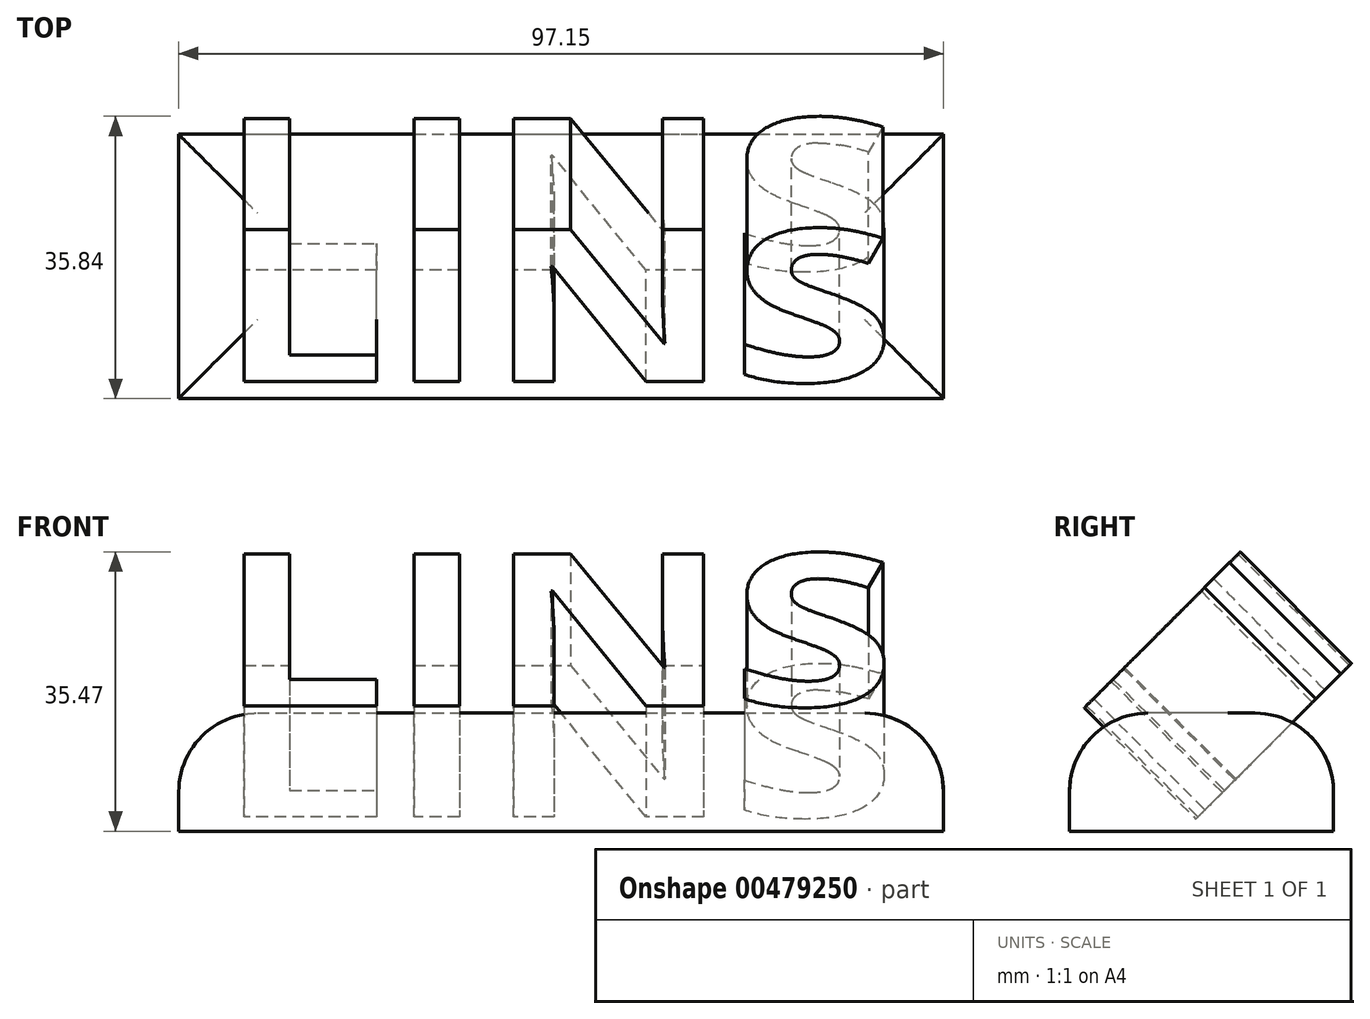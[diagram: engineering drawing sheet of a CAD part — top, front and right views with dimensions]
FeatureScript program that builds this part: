
annotation { "Feature Type Name" : "Feature", "Feature Type Description" : "" }
export const myFeature = defineFeature(function(context is Context, id is Id, definition is map)
    precondition{}
    {
        {
            var Q0;
            Q0=qCreatedBy(makeId("Top.planeOp"),FACE);
            var sketch = newSketch(context, id + "F0", { "sketchPlane" : qUnion([Q0])});
            skText(sketch, "E0", { "text": "LINS", "fontName": "OpenSans-Bold.ttf"});
            const initialGuessF0  = {"E0": [-0.04957, -0.04822, 1, 0, 0.02747]};
            skSetInitialGuess(sketch, initialGuessF0);
            skSolve(sketch);
        }
        {
            var Q0;
            Q0 = qSketchRegion(id + "F0", true);
            extrude(context, id + "F1", {"entities" : qUnion([Q0]), "depth" : 20 * mm});
        }
        {
            var Q0;
            Q0=qCreatedBy(makeId("Top.planeOp"),FACE);
            var sketch = newSketch(context, id + "F2", { "sketchPlane" : qUnion([Q0])});
            skLineSegment(sketch, "E1.bottom", {"start": v(-44.06, 21.02) * mm, "end": v(53.1, 21.02) * mm});
            skLineSegment(sketch, "E1.top", {"start": v(-44.06, -12.54) * mm, "end": v(53.1, -12.54) * mm});
            skLineSegment(sketch, "E1.left", {"start": v(-44.06, 21.02) * mm, "end": v(-44.06, -12.54) * mm});
            skLineSegment(sketch, "E1.right", {"start": v(53.1, 21.02) * mm, "end": v(53.1, -12.54) * mm});
            skSolve(sketch);
        }
        {
            var Q0;
            Q0=makeQuery(id+"F2.imprint","IMPRINT",FACE,{"disambiguationData":[TD([[makeQuery(id+"F2.imprint","IMPRINT",EDGE,{"derivedFrom":sQuery(id+"F2.wireOp",EDGE,"E1.bottom")}),-1.0]])]});
            extrude(context, id + "F3", {"entities" : qUnion([Q0]), "depth" : 15 * mm});
        }
        {
            var Q0;
            Q0=makeQuery(id+"F3.opExtrude","CAP_EDGE",EDGE,{"disambiguationData":[OSD([sQuery(id+"F2.wireOp",EDGE,"E1.left")])],"isStart":false});
            var Q1;
            Q1=makeQuery(id+"F3.opExtrude","CAP_EDGE",EDGE,{"disambiguationData":[OSD([sQuery(id+"F2.wireOp",EDGE,"E1.bottom")])],"isStart":false});
            var Q2;
            Q2=makeQuery(id+"F3.opExtrude","CAP_EDGE",EDGE,{"disambiguationData":[OSD([sQuery(id+"F2.wireOp",EDGE,"E1.right")])],"isStart":false});
            var Q3;
            Q3=makeQuery(id+"F3.opExtrude","CAP_EDGE",EDGE,{"disambiguationData":[OSD([sQuery(id+"F2.wireOp",EDGE,"E1.top")])],"isStart":false});
            fillet(context, id + "F4", {"entities" : qUnion([Q0, Q1, Q2, Q3]), "radius" : 10 * mm, "tangentPropagation" : true, "allowEdgeOverflow" : false});
        }
        {
            var Q0;
            Q0=makeQuery(id+"F1.opExtrude","SWEPT_BODY",BODY,{"disambiguationData":[OSD([sQuery(id+"F0.wireOp",EDGE,"E0.sketch_text.stroke-0"),sQuery(id+"F0.wireOp",EDGE,"E0.sketch_text.stroke-1"),sQuery(id+"F0.wireOp",EDGE,"E0.sketch_text.stroke-2"),sQuery(id+"F0.wireOp",EDGE,"E0.sketch_text.stroke-3"),sQuery(id+"F0.wireOp",EDGE,"E0.sketch_text.stroke-4"),sQuery(id+"F0.wireOp",EDGE,"E0.sketch_text.stroke-5"),sQuery(id+"F0.wireOp",EDGE,"E0.sketch_text.stroke-6"),sQuery(id+"F0.wireOp",EDGE,"E0.sketch_text.stroke-7"),sQuery(id+"F0.wireOp",EDGE,"E0.sketch_text.stroke-8"),sQuery(id+"F0.wireOp",EDGE,"E0.sketch_text.stroke-9"),sQuery(id+"F0.wireOp",EDGE,"E0.sketch_text.stroke-10"),sQuery(id+"F0.wireOp",EDGE,"E0.sketch_text.stroke-11"),sQuery(id+"F0.wireOp",EDGE,"E0.sketch_text.stroke-12"),sQuery(id+"F0.wireOp",EDGE,"E0.sketch_text.stroke-13")])]});
            var Q1;
            Q1=makeQuery(id+"F1.opExtrude","SWEPT_BODY",BODY,{"disambiguationData":[OSD([sQuery(id+"F0.wireOp",EDGE,"E0.sketch_text.stroke-14"),sQuery(id+"F0.wireOp",EDGE,"E0.sketch_text.stroke-15"),sQuery(id+"F0.wireOp",EDGE,"E0.sketch_text.stroke-16"),sQuery(id+"F0.wireOp",EDGE,"E0.sketch_text.stroke-17")])]});
            var Q2;
            Q2=makeQuery(id+"F1.opExtrude","SWEPT_BODY",BODY,{"disambiguationData":[OSD([sQuery(id+"F0.wireOp",EDGE,"E0.sketch_text.stroke-18"),sQuery(id+"F0.wireOp",EDGE,"E0.sketch_text.stroke-19"),sQuery(id+"F0.wireOp",EDGE,"E0.sketch_text.stroke-20"),sQuery(id+"F0.wireOp",EDGE,"E0.sketch_text.stroke-21"),sQuery(id+"F0.wireOp",EDGE,"E0.sketch_text.stroke-22"),sQuery(id+"F0.wireOp",EDGE,"E0.sketch_text.stroke-23"),sQuery(id+"F0.wireOp",EDGE,"E0.sketch_text.stroke-24"),sQuery(id+"F0.wireOp",EDGE,"E0.sketch_text.stroke-25"),sQuery(id+"F0.wireOp",EDGE,"E0.sketch_text.stroke-26"),sQuery(id+"F0.wireOp",EDGE,"E0.sketch_text.stroke-27"),sQuery(id+"F0.wireOp",EDGE,"E0.sketch_text.stroke-28"),sQuery(id+"F0.wireOp",EDGE,"E0.sketch_text.stroke-29"),sQuery(id+"F0.wireOp",EDGE,"E0.sketch_text.stroke-30"),sQuery(id+"F0.wireOp",EDGE,"E0.sketch_text.stroke-31"),sQuery(id+"F0.wireOp",EDGE,"E0.sketch_text.stroke-32")])]});
            var Q3;
            Q3=makeQuery(id+"F1.opExtrude","SWEPT_BODY",BODY,{"disambiguationData":[OSD([sQuery(id+"F0.wireOp",EDGE,"E0.sketch_text.stroke-33"),sQuery(id+"F0.wireOp",EDGE,"E0.sketch_text.stroke-34"),sQuery(id+"F0.wireOp",EDGE,"E0.sketch_text.stroke-35"),sQuery(id+"F0.wireOp",EDGE,"E0.sketch_text.stroke-36"),sQuery(id+"F0.wireOp",EDGE,"E0.sketch_text.stroke-37"),sQuery(id+"F0.wireOp",EDGE,"E0.sketch_text.stroke-38"),sQuery(id+"F0.wireOp",EDGE,"E0.sketch_text.stroke-39"),sQuery(id+"F0.wireOp",EDGE,"E0.sketch_text.stroke-40"),sQuery(id+"F0.wireOp",EDGE,"E0.sketch_text.stroke-41"),sQuery(id+"F0.wireOp",EDGE,"E0.sketch_text.stroke-42"),sQuery(id+"F0.wireOp",EDGE,"E0.sketch_text.stroke-43"),sQuery(id+"F0.wireOp",EDGE,"E0.sketch_text.stroke-44"),sQuery(id+"F0.wireOp",EDGE,"E0.sketch_text.stroke-45")])]});
            var Q4;
            Q4=makeQuery(id+"F1.opExtrude","SWEPT_BODY",BODY,{"disambiguationData":[OSD([sQuery(id+"F0.wireOp",EDGE,"E0.sketch_text.stroke-6"),sQuery(id+"F0.wireOp",EDGE,"E0.sketch_text.stroke-7"),sQuery(id+"F0.wireOp",EDGE,"E0.sketch_text.stroke-8"),sQuery(id+"F0.wireOp",EDGE,"E0.sketch_text.stroke-9")])]});
            transform(context, id + "F5", {"entities" : qUnion([Q0, Q1, Q2, Q3, Q4]), "transformType" : TransformType.TRANSLATION_3D, "dx" : 5.33 * mm, "dy" : 37.85 * mm, "dz" : 0 * mm, "makeCopy" : false});
        }
        {
            var Q0;
            Q0=makeQuery(id+"F1.opExtrude","SWEPT_BODY",BODY,{"disambiguationData":[OSD([sQuery(id+"F0.wireOp",EDGE,"E0.sketch_text.stroke-0"),sQuery(id+"F0.wireOp",EDGE,"E0.sketch_text.stroke-1"),sQuery(id+"F0.wireOp",EDGE,"E0.sketch_text.stroke-2"),sQuery(id+"F0.wireOp",EDGE,"E0.sketch_text.stroke-3"),sQuery(id+"F0.wireOp",EDGE,"E0.sketch_text.stroke-4"),sQuery(id+"F0.wireOp",EDGE,"E0.sketch_text.stroke-5"),sQuery(id+"F0.wireOp",EDGE,"E0.sketch_text.stroke-6"),sQuery(id+"F0.wireOp",EDGE,"E0.sketch_text.stroke-7"),sQuery(id+"F0.wireOp",EDGE,"E0.sketch_text.stroke-8"),sQuery(id+"F0.wireOp",EDGE,"E0.sketch_text.stroke-9"),sQuery(id+"F0.wireOp",EDGE,"E0.sketch_text.stroke-10"),sQuery(id+"F0.wireOp",EDGE,"E0.sketch_text.stroke-11"),sQuery(id+"F0.wireOp",EDGE,"E0.sketch_text.stroke-12"),sQuery(id+"F0.wireOp",EDGE,"E0.sketch_text.stroke-13")])]});
            var Q1;
            Q1=makeQuery(id+"F1.opExtrude","SWEPT_BODY",BODY,{"disambiguationData":[OSD([sQuery(id+"F0.wireOp",EDGE,"E0.sketch_text.stroke-14"),sQuery(id+"F0.wireOp",EDGE,"E0.sketch_text.stroke-15"),sQuery(id+"F0.wireOp",EDGE,"E0.sketch_text.stroke-16"),sQuery(id+"F0.wireOp",EDGE,"E0.sketch_text.stroke-17")])]});
            var Q2;
            Q2=makeQuery(id+"F1.opExtrude","SWEPT_BODY",BODY,{"disambiguationData":[OSD([sQuery(id+"F0.wireOp",EDGE,"E0.sketch_text.stroke-18"),sQuery(id+"F0.wireOp",EDGE,"E0.sketch_text.stroke-19"),sQuery(id+"F0.wireOp",EDGE,"E0.sketch_text.stroke-20"),sQuery(id+"F0.wireOp",EDGE,"E0.sketch_text.stroke-21"),sQuery(id+"F0.wireOp",EDGE,"E0.sketch_text.stroke-22"),sQuery(id+"F0.wireOp",EDGE,"E0.sketch_text.stroke-23"),sQuery(id+"F0.wireOp",EDGE,"E0.sketch_text.stroke-24"),sQuery(id+"F0.wireOp",EDGE,"E0.sketch_text.stroke-25"),sQuery(id+"F0.wireOp",EDGE,"E0.sketch_text.stroke-26"),sQuery(id+"F0.wireOp",EDGE,"E0.sketch_text.stroke-27"),sQuery(id+"F0.wireOp",EDGE,"E0.sketch_text.stroke-28"),sQuery(id+"F0.wireOp",EDGE,"E0.sketch_text.stroke-29"),sQuery(id+"F0.wireOp",EDGE,"E0.sketch_text.stroke-30"),sQuery(id+"F0.wireOp",EDGE,"E0.sketch_text.stroke-31"),sQuery(id+"F0.wireOp",EDGE,"E0.sketch_text.stroke-32")])]});
            var Q3;
            Q3=makeQuery(id+"F1.opExtrude","SWEPT_BODY",BODY,{"disambiguationData":[OSD([sQuery(id+"F0.wireOp",EDGE,"E0.sketch_text.stroke-33"),sQuery(id+"F0.wireOp",EDGE,"E0.sketch_text.stroke-34"),sQuery(id+"F0.wireOp",EDGE,"E0.sketch_text.stroke-35"),sQuery(id+"F0.wireOp",EDGE,"E0.sketch_text.stroke-36"),sQuery(id+"F0.wireOp",EDGE,"E0.sketch_text.stroke-37"),sQuery(id+"F0.wireOp",EDGE,"E0.sketch_text.stroke-38"),sQuery(id+"F0.wireOp",EDGE,"E0.sketch_text.stroke-39"),sQuery(id+"F0.wireOp",EDGE,"E0.sketch_text.stroke-40"),sQuery(id+"F0.wireOp",EDGE,"E0.sketch_text.stroke-41"),sQuery(id+"F0.wireOp",EDGE,"E0.sketch_text.stroke-42"),sQuery(id+"F0.wireOp",EDGE,"E0.sketch_text.stroke-43"),sQuery(id+"F0.wireOp",EDGE,"E0.sketch_text.stroke-44"),sQuery(id+"F0.wireOp",EDGE,"E0.sketch_text.stroke-45")])]});
            var Q4;
            Q4=makeQuery(id+"F1.opExtrude","SWEPT_BODY",BODY,{"disambiguationData":[OSD([sQuery(id+"F0.wireOp",EDGE,"E0.sketch_text.stroke-6"),sQuery(id+"F0.wireOp",EDGE,"E0.sketch_text.stroke-7"),sQuery(id+"F0.wireOp",EDGE,"E0.sketch_text.stroke-8"),sQuery(id+"F0.wireOp",EDGE,"E0.sketch_text.stroke-9")])]});
            var Q5;
            Q5=makeQuery(id+"F1.opExtrude","CAP_EDGE",EDGE,{"disambiguationData":[OSD([sQuery(id+"F0.wireOp",EDGE,"E0.sketch_text.stroke-5")])],"isStart":false});
            transform(context, id + "F6", {"entities" : qUnion([Q0, Q1, Q2, Q3, Q4]), "transformType" : TransformType.ROTATION, "transformAxis" : qUnion([Q5]), "angle" : 45 * degree, "oppositeDirection" : true, "makeCopy" : false});
        }
        {
            var Q0;
            Q0=makeQuery(id+"F1.opExtrude","SWEPT_BODY",BODY,{"disambiguationData":[OSD([sQuery(id+"F0.wireOp",EDGE,"E0.sketch_text.stroke-0"),sQuery(id+"F0.wireOp",EDGE,"E0.sketch_text.stroke-1"),sQuery(id+"F0.wireOp",EDGE,"E0.sketch_text.stroke-2"),sQuery(id+"F0.wireOp",EDGE,"E0.sketch_text.stroke-3"),sQuery(id+"F0.wireOp",EDGE,"E0.sketch_text.stroke-4"),sQuery(id+"F0.wireOp",EDGE,"E0.sketch_text.stroke-5"),sQuery(id+"F0.wireOp",EDGE,"E0.sketch_text.stroke-6"),sQuery(id+"F0.wireOp",EDGE,"E0.sketch_text.stroke-7"),sQuery(id+"F0.wireOp",EDGE,"E0.sketch_text.stroke-8"),sQuery(id+"F0.wireOp",EDGE,"E0.sketch_text.stroke-9"),sQuery(id+"F0.wireOp",EDGE,"E0.sketch_text.stroke-10"),sQuery(id+"F0.wireOp",EDGE,"E0.sketch_text.stroke-11"),sQuery(id+"F0.wireOp",EDGE,"E0.sketch_text.stroke-12"),sQuery(id+"F0.wireOp",EDGE,"E0.sketch_text.stroke-13")])]});
            var Q1;
            Q1=makeQuery(id+"F1.opExtrude","SWEPT_BODY",BODY,{"disambiguationData":[OSD([sQuery(id+"F0.wireOp",EDGE,"E0.sketch_text.stroke-14"),sQuery(id+"F0.wireOp",EDGE,"E0.sketch_text.stroke-15"),sQuery(id+"F0.wireOp",EDGE,"E0.sketch_text.stroke-16"),sQuery(id+"F0.wireOp",EDGE,"E0.sketch_text.stroke-17")])]});
            var Q2;
            Q2=makeQuery(id+"F1.opExtrude","SWEPT_BODY",BODY,{"disambiguationData":[OSD([sQuery(id+"F0.wireOp",EDGE,"E0.sketch_text.stroke-18"),sQuery(id+"F0.wireOp",EDGE,"E0.sketch_text.stroke-19"),sQuery(id+"F0.wireOp",EDGE,"E0.sketch_text.stroke-20"),sQuery(id+"F0.wireOp",EDGE,"E0.sketch_text.stroke-21"),sQuery(id+"F0.wireOp",EDGE,"E0.sketch_text.stroke-22"),sQuery(id+"F0.wireOp",EDGE,"E0.sketch_text.stroke-23"),sQuery(id+"F0.wireOp",EDGE,"E0.sketch_text.stroke-24"),sQuery(id+"F0.wireOp",EDGE,"E0.sketch_text.stroke-25"),sQuery(id+"F0.wireOp",EDGE,"E0.sketch_text.stroke-26"),sQuery(id+"F0.wireOp",EDGE,"E0.sketch_text.stroke-27"),sQuery(id+"F0.wireOp",EDGE,"E0.sketch_text.stroke-28"),sQuery(id+"F0.wireOp",EDGE,"E0.sketch_text.stroke-29"),sQuery(id+"F0.wireOp",EDGE,"E0.sketch_text.stroke-30"),sQuery(id+"F0.wireOp",EDGE,"E0.sketch_text.stroke-31"),sQuery(id+"F0.wireOp",EDGE,"E0.sketch_text.stroke-32")])]});
            var Q3;
            Q3=makeQuery(id+"F1.opExtrude","SWEPT_BODY",BODY,{"disambiguationData":[OSD([sQuery(id+"F0.wireOp",EDGE,"E0.sketch_text.stroke-33"),sQuery(id+"F0.wireOp",EDGE,"E0.sketch_text.stroke-34"),sQuery(id+"F0.wireOp",EDGE,"E0.sketch_text.stroke-35"),sQuery(id+"F0.wireOp",EDGE,"E0.sketch_text.stroke-36"),sQuery(id+"F0.wireOp",EDGE,"E0.sketch_text.stroke-37"),sQuery(id+"F0.wireOp",EDGE,"E0.sketch_text.stroke-38"),sQuery(id+"F0.wireOp",EDGE,"E0.sketch_text.stroke-39"),sQuery(id+"F0.wireOp",EDGE,"E0.sketch_text.stroke-40"),sQuery(id+"F0.wireOp",EDGE,"E0.sketch_text.stroke-41"),sQuery(id+"F0.wireOp",EDGE,"E0.sketch_text.stroke-42"),sQuery(id+"F0.wireOp",EDGE,"E0.sketch_text.stroke-43"),sQuery(id+"F0.wireOp",EDGE,"E0.sketch_text.stroke-44"),sQuery(id+"F0.wireOp",EDGE,"E0.sketch_text.stroke-45")])]});
            var Q4;
            Q4=makeQuery(id+"F1.opExtrude","SWEPT_BODY",BODY,{"disambiguationData":[OSD([sQuery(id+"F0.wireOp",EDGE,"E0.sketch_text.stroke-6"),sQuery(id+"F0.wireOp",EDGE,"E0.sketch_text.stroke-7"),sQuery(id+"F0.wireOp",EDGE,"E0.sketch_text.stroke-8"),sQuery(id+"F0.wireOp",EDGE,"E0.sketch_text.stroke-9")])]});
            transform(context, id + "F7", {"entities" : qUnion([Q0, Q1, Q2, Q3, Q4]), "transformType" : TransformType.TRANSLATION_3D, "dx" : 5.08 * mm, "dy" : 0 * mm, "dz" : -4.06 * mm, "makeCopy" : false});
        }
    });
